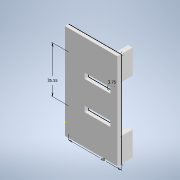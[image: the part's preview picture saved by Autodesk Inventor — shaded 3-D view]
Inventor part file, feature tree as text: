
AUTODESK INVENTOR PART (.ipt)
format: ipt  version: 2022 (Build 260153070, 153G)  size: 142,848 bytes
history: native  units: mm
features: other x9, reference x6, extrude x3, sketch x2, plane x2
ambient origin geometry x8: Origin, YZ Plane, XZ Plane, XY Plane, X Axis, Y Axis, Z Axis, Center Point
bodies: Solid1 (feature_tree)
feature tree (22):
  sketch  "Sketch1"  dims[d1=35.55mm d2=1.0mm]
  extrude  "Extrusion1"  Depth=35.55mm
  plane  "Work Plane1"
  extrude  "Extrusion2"  Depth=40.0mm
  plane  "Work Plane2"
  extrude  "Extrusion3"  Depth=2.75mm TaperAngle=0.0deg
  reference  "Reference1"
  reference  "Reference2"
  reference  "Reference4"
  reference  "Reference5"
  reference  "Reference6"
  sketch  "Sketch3"  dims[d3=3.75mm d4=40.0mm d5=2.75mm d6=0.0mm d7=2.75mm d8=0.0mm d9=1.0mm d10=17.75mm d11=0.0mm]
  reference  "Reference8"
  other  "<userpath> laptop\Desktop\SumoBot\FullBot.iam"
  other  "FullBot.iam"
  other  "MotorEncoderAssembly_MIR:1"
  other  "TT encoder disk_MIR:1"
  other  "MotorEncoderAssembly:1"
  other  "TT motor output:1"
  other  "MotorEncoderBracket:1"
  other  "AssemblyV3:1"
  other  "SRM-12-06A:1"
